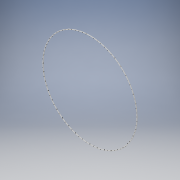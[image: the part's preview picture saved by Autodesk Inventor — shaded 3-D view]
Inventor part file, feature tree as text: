
AUTODESK INVENTOR PART (.ipt)
format: ipt  version: 2018 (Build 220112000, 112)  size: 598,528 bytes
history: native  units: in
note: dims shown in document units (in); Inventor stores cm internally (conversion verified against a paired STEP export)
features: extrude x3, sketch x3, pattern_circular x2, fillet x1
ambient origin geometry x8: Origin, YZ Plane, XZ Plane, XY Plane, X Axis, Y Axis, Z Axis, Center Point
bodies: Solid1 (feature_tree)
feature tree (9):
  extrude  "Extrusion1"  Depth=1786.0in
  fillet  "Fillet2"  Radius=1814.0in
  extrude  "Extrusion2"  Depth=7.0in
  pattern_circular  "Circular Pattern1"  Count=2286  [1 undecoded]
  extrude  "Extrusion3"  Depth=900.0in TaperAngle=360.0deg
  pattern_circular  "Circular Pattern2"  [2 undecoded]
  sketch  "Sketch1"  dims[d0=1800.0in d1=1786.0in d2=1814.0in]
  sketch  "Sketch2"  dims[d3=14.0in d4=0.0in d6=7.0in]
  sketch  "Sketch3"  dims[d7=10.0in d8=900.0in d9=0.0in d10=15.748in d11=360.0deg d14=0.0309in d15=6.0in d16=1800.0in d17=900.0in d18=0.0in d19=15.748in d20=360.0deg]
note: 3 required parameter values undecoded (feature->parameter linkage not recoverable at this tier; creation-order binding heuristic only, values carry confidence <= 0.55)
